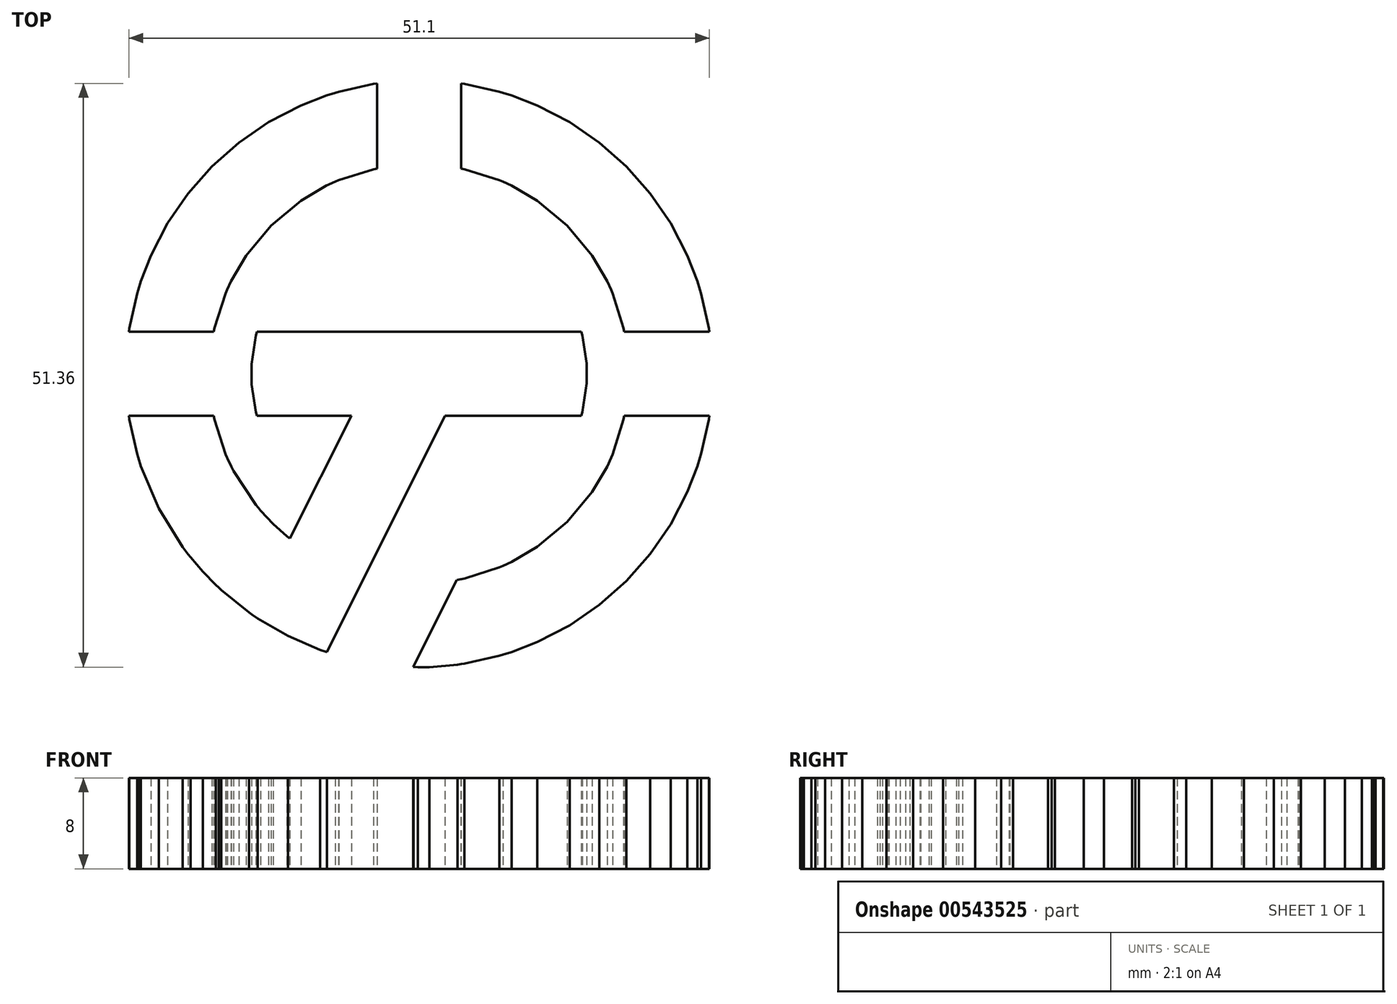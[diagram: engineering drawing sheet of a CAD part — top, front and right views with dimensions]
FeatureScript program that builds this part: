
annotation { "Feature Type Name" : "Feature", "Feature Type Description" : "" }
export const myFeature = defineFeature(function(context is Context, id is Id, definition is map)
    precondition{}
    {
        {
            var Q0;
            Q0=qCreatedBy(makeId("Top.planeOp"),FACE);
            var sketch = newSketch(context, id + "F0", { "sketchPlane" : qUnion([Q0])});
            skLineSegment(sketch, "E0", {"start": v(16.9, -7.24) * mm, "end": v(16.55, -8.03) * mm});
            skLineSegment(sketch, "E1", {"start": v(16.55, -8.03) * mm, "end": v(15.22, -10.26) * mm});
            skLineSegment(sketch, "E2", {"start": v(15.22, -10.26) * mm, "end": v(13.03, -12.9) * mm});
            skLineSegment(sketch, "E3", {"start": v(13.03, -12.9) * mm, "end": v(10.4, -15.09) * mm});
            skLineSegment(sketch, "E4", {"start": v(10.4, -15.09) * mm, "end": v(8.16, -16.42) * mm});
            skLineSegment(sketch, "E5", {"start": v(8.16, -16.42) * mm, "end": v(7.37, -16.76) * mm});
            skLineSegment(sketch, "E6", {"start": v(7.37, -16.76) * mm, "end": v(7.08, -16.9) * mm});
            skLineSegment(sketch, "E7", {"start": v(7.08, -16.9) * mm, "end": v(4, -17.87) * mm});
            skLineSegment(sketch, "E8", {"start": v(4, -17.87) * mm, "end": v(3.69, -17.93) * mm});
            skLineSegment(sketch, "E9", {"start": v(3.69, -17.93) * mm, "end": v(3.66, -17.94) * mm});
            skLineSegment(sketch, "E10", {"start": v(3.66, -17.94) * mm, "end": v(3.34, -18) * mm});
            skLineSegment(sketch, "E11", {"start": v(3.34, -18) * mm, "end": v(3.31, -18) * mm});
            skLineSegment(sketch, "E12", {"start": v(3.31, -18) * mm, "end": v(-0.53, -25.67) * mm});
            skLineSegment(sketch, "E13", {"start": v(-0.53, -25.67) * mm, "end": v(-0.49, -25.67) * mm});
            skLineSegment(sketch, "E14", {"start": v(-0.49, -25.67) * mm, "end": v(-0.12, -25.68) * mm});
            skLineSegment(sketch, "E15", {"start": v(-0.12, -25.68) * mm, "end": v(0, -25.68) * mm});
            skLineSegment(sketch, "E16", {"start": v(0, -25.68) * mm, "end": v(0.92, -25.68) * mm});
            skLineSegment(sketch, "E17", {"start": v(0.92, -25.68) * mm, "end": v(3.39, -25.46) * mm});
            skLineSegment(sketch, "E18", {"start": v(3.39, -25.46) * mm, "end": v(3.69, -25.42) * mm});
            skLineSegment(sketch, "E19", {"start": v(3.69, -25.42) * mm, "end": v(4, -25.37) * mm});
            skLineSegment(sketch, "E20", {"start": v(4, -25.37) * mm, "end": v(7.07, -24.69) * mm});
            skLineSegment(sketch, "E21", {"start": v(7.07, -24.69) * mm, "end": v(7.37, -24.6) * mm});
            skLineSegment(sketch, "E22", {"start": v(7.37, -24.6) * mm, "end": v(8.15, -24.37) * mm});
            skLineSegment(sketch, "E23", {"start": v(8.15, -24.37) * mm, "end": v(10.4, -23.48) * mm});
            skLineSegment(sketch, "E24", {"start": v(10.4, -23.48) * mm, "end": v(13.25, -22) * mm});
            skLineSegment(sketch, "E25", {"start": v(13.25, -22) * mm, "end": v(15.87, -20.21) * mm});
            skLineSegment(sketch, "E26", {"start": v(15.87, -20.21) * mm, "end": v(18.24, -18.1) * mm});
            skLineSegment(sketch, "E27", {"start": v(18.24, -18.1) * mm, "end": v(20.34, -15.73) * mm});
            skLineSegment(sketch, "E28", {"start": v(20.34, -15.73) * mm, "end": v(22.14, -13.11) * mm});
            skLineSegment(sketch, "E29", {"start": v(22.14, -13.11) * mm, "end": v(23.61, -10.27) * mm});
            skLineSegment(sketch, "E30", {"start": v(23.61, -10.27) * mm, "end": v(24.5, -8.02) * mm});
            skLineSegment(sketch, "E31", {"start": v(24.5, -8.02) * mm, "end": v(24.73, -7.24) * mm});
            skLineSegment(sketch, "E32", {"start": v(24.73, -7.24) * mm, "end": v(24.82, -6.94) * mm});
            skLineSegment(sketch, "E33", {"start": v(24.82, -6.94) * mm, "end": v(25.5, -3.87) * mm});
            skLineSegment(sketch, "E34", {"start": v(25.5, -3.87) * mm, "end": v(25.55, -3.56) * mm});
            skLineSegment(sketch, "E35", {"start": v(25.55, -3.56) * mm, "end": v(18.07, -3.56) * mm});
            skLineSegment(sketch, "E36", {"start": v(18.07, -3.56) * mm, "end": v(18, -3.88) * mm});
            skLineSegment(sketch, "E37", {"start": v(18, -3.88) * mm, "end": v(17.02, -6.95) * mm});
            skLineSegment(sketch, "E38", {"start": v(17.02, -6.95) * mm, "end": v(16.9, -7.24) * mm});
            skLineSegment(sketch, "E39", {"start": v(16.9, 7.5) * mm, "end": v(17.02, 7.21) * mm});
            skLineSegment(sketch, "E40", {"start": v(17.02, 7.21) * mm, "end": v(18, 4.14) * mm});
            skLineSegment(sketch, "E41", {"start": v(18, 4.14) * mm, "end": v(18.07, 3.82) * mm});
            skLineSegment(sketch, "E42", {"start": v(18.07, 3.82) * mm, "end": v(25.55, 3.82) * mm});
            skLineSegment(sketch, "E43", {"start": v(25.55, 3.82) * mm, "end": v(25.5, 4.13) * mm});
            skLineSegment(sketch, "E44", {"start": v(25.5, 4.13) * mm, "end": v(24.82, 7.2) * mm});
            skLineSegment(sketch, "E45", {"start": v(24.82, 7.2) * mm, "end": v(24.73, 7.5) * mm});
            skLineSegment(sketch, "E46", {"start": v(24.73, 7.5) * mm, "end": v(24.5, 8.28) * mm});
            skLineSegment(sketch, "E47", {"start": v(24.5, 8.28) * mm, "end": v(23.61, 10.54) * mm});
            skLineSegment(sketch, "E48", {"start": v(23.61, 10.54) * mm, "end": v(22.14, 13.38) * mm});
            skLineSegment(sketch, "E49", {"start": v(22.14, 13.38) * mm, "end": v(20.34, 16) * mm});
            skLineSegment(sketch, "E50", {"start": v(20.34, 16) * mm, "end": v(18.24, 18.37) * mm});
            skLineSegment(sketch, "E51", {"start": v(18.24, 18.37) * mm, "end": v(15.87, 20.47) * mm});
            skLineSegment(sketch, "E52", {"start": v(15.87, 20.47) * mm, "end": v(13.25, 22.27) * mm});
            skLineSegment(sketch, "E53", {"start": v(13.25, 22.27) * mm, "end": v(10.4, 23.74) * mm});
            skLineSegment(sketch, "E54", {"start": v(10.4, 23.74) * mm, "end": v(8.15, 24.63) * mm});
            skLineSegment(sketch, "E55", {"start": v(8.15, 24.63) * mm, "end": v(7.37, 24.86) * mm});
            skLineSegment(sketch, "E56", {"start": v(7.37, 24.86) * mm, "end": v(7.07, 24.95) * mm});
            skLineSegment(sketch, "E57", {"start": v(7.07, 24.95) * mm, "end": v(4, 25.63) * mm});
            skLineSegment(sketch, "E58", {"start": v(4, 25.63) * mm, "end": v(3.69, 25.68) * mm});
            skLineSegment(sketch, "E59", {"start": v(3.69, 25.68) * mm, "end": v(3.69, 18.2) * mm});
            skLineSegment(sketch, "E60", {"start": v(3.69, 18.2) * mm, "end": v(4, 18.13) * mm});
            skLineSegment(sketch, "E61", {"start": v(4, 18.13) * mm, "end": v(7.08, 17.16) * mm});
            skLineSegment(sketch, "E62", {"start": v(7.08, 17.16) * mm, "end": v(7.37, 17.03) * mm});
            skLineSegment(sketch, "E63", {"start": v(7.37, 17.03) * mm, "end": v(8.16, 16.68) * mm});
            skLineSegment(sketch, "E64", {"start": v(8.16, 16.68) * mm, "end": v(10.4, 15.35) * mm});
            skLineSegment(sketch, "E65", {"start": v(10.4, 15.35) * mm, "end": v(13.03, 13.16) * mm});
            skLineSegment(sketch, "E66", {"start": v(13.03, 13.16) * mm, "end": v(15.22, 10.52) * mm});
            skLineSegment(sketch, "E67", {"start": v(15.22, 10.52) * mm, "end": v(16.55, 8.3) * mm});
            skLineSegment(sketch, "E68", {"start": v(16.55, 8.3) * mm, "end": v(16.9, 7.5) * mm});
            skLineSegment(sketch, "E69", {"start": v(2.29, -3.55) * mm, "end": v(14.28, -3.55) * mm});
            skLineSegment(sketch, "E70", {"start": v(14.28, -3.55) * mm, "end": v(14.36, -3.26) * mm});
            skLineSegment(sketch, "E71", {"start": v(14.36, -3.26) * mm, "end": v(14.75, -0.72) * mm});
            skLineSegment(sketch, "E72", {"start": v(14.75, -0.72) * mm, "end": v(14.75, 0.13) * mm});
            skLineSegment(sketch, "E73", {"start": v(14.75, 0.13) * mm, "end": v(14.75, 1.05) * mm});
            skLineSegment(sketch, "E74", {"start": v(14.75, 1.05) * mm, "end": v(14.36, 3.52) * mm});
            skLineSegment(sketch, "E75", {"start": v(14.36, 3.52) * mm, "end": v(14.28, 3.82) * mm});
            skLineSegment(sketch, "E76", {"start": v(14.28, 3.82) * mm, "end": v(-14.28, 3.82) * mm});
            skLineSegment(sketch, "E77", {"start": v(-14.28, 3.82) * mm, "end": v(-14.36, 3.52) * mm});
            skLineSegment(sketch, "E78", {"start": v(-14.36, 3.52) * mm, "end": v(-14.75, 0.98) * mm});
            skLineSegment(sketch, "E79", {"start": v(-14.75, 0.98) * mm, "end": v(-14.75, 0.13) * mm});
            skLineSegment(sketch, "E80", {"start": v(-14.75, 0.13) * mm, "end": v(-14.75, -0.8) * mm});
            skLineSegment(sketch, "E81", {"start": v(-14.75, -0.8) * mm, "end": v(-14.36, -3.26) * mm});
            skLineSegment(sketch, "E82", {"start": v(-14.36, -3.26) * mm, "end": v(-14.28, -3.55) * mm});
            skLineSegment(sketch, "E83", {"start": v(-14.28, -3.55) * mm, "end": v(-5.96, -3.55) * mm});
            skLineSegment(sketch, "E84", {"start": v(-5.96, -3.55) * mm, "end": v(-11.37, -14.36) * mm});
            skLineSegment(sketch, "E85", {"start": v(-11.37, -14.36) * mm, "end": v(-11.63, -14.16) * mm});
            skLineSegment(sketch, "E86", {"start": v(-11.63, -14.16) * mm, "end": v(-12.83, -13.1) * mm});
            skLineSegment(sketch, "E87", {"start": v(-12.83, -13.1) * mm, "end": v(-13.94, -11.92) * mm});
            skLineSegment(sketch, "E88", {"start": v(-13.94, -11.92) * mm, "end": v(-14.15, -11.68) * mm});
            skLineSegment(sketch, "E89", {"start": v(-14.15, -11.68) * mm, "end": v(-14.38, -11.4) * mm});
            skLineSegment(sketch, "E90", {"start": v(-14.38, -11.4) * mm, "end": v(-16.33, -8.42) * mm});
            skLineSegment(sketch, "E91", {"start": v(-16.33, -8.42) * mm, "end": v(-16.5, -8.1) * mm});
            skLineSegment(sketch, "E92", {"start": v(-16.5, -8.1) * mm, "end": v(-16.53, -8.03) * mm});
            skLineSegment(sketch, "E93", {"start": v(-16.53, -8.03) * mm, "end": v(-16.86, -7.31) * mm});
            skLineSegment(sketch, "E94", {"start": v(-16.86, -7.31) * mm, "end": v(-16.9, -7.24) * mm});
            skLineSegment(sketch, "E95", {"start": v(-16.9, -7.24) * mm, "end": v(-17.02, -6.95) * mm});
            skLineSegment(sketch, "E96", {"start": v(-17.02, -6.95) * mm, "end": v(-18, -3.87) * mm});
            skLineSegment(sketch, "E97", {"start": v(-18, -3.87) * mm, "end": v(-18.07, -3.55) * mm});
            skLineSegment(sketch, "E98", {"start": v(-18.07, -3.55) * mm, "end": v(-25.55, -3.55) * mm});
            skLineSegment(sketch, "E99", {"start": v(-25.55, -3.55) * mm, "end": v(-25.5, -3.87) * mm});
            skLineSegment(sketch, "E100", {"start": v(-25.5, -3.87) * mm, "end": v(-24.82, -6.94) * mm});
            skLineSegment(sketch, "E101", {"start": v(-24.82, -6.94) * mm, "end": v(-24.73, -7.24) * mm});
            skLineSegment(sketch, "E102", {"start": v(-24.73, -7.24) * mm, "end": v(-24.5, -8.03) * mm});
            skLineSegment(sketch, "E103", {"start": v(-24.5, -8.03) * mm, "end": v(-22.91, -11.73) * mm});
            skLineSegment(sketch, "E104", {"start": v(-22.91, -11.73) * mm, "end": v(-20.81, -15.13) * mm});
            skLineSegment(sketch, "E105", {"start": v(-20.81, -15.13) * mm, "end": v(-20.32, -15.76) * mm});
            skLineSegment(sketch, "E106", {"start": v(-20.32, -15.76) * mm, "end": v(-20.12, -16.02) * mm});
            skLineSegment(sketch, "E107", {"start": v(-20.12, -16.02) * mm, "end": v(-19.04, -17.27) * mm});
            skLineSegment(sketch, "E108", {"start": v(-19.04, -17.27) * mm, "end": v(-17.9, -18.45) * mm});
            skLineSegment(sketch, "E109", {"start": v(-17.9, -18.45) * mm, "end": v(-17.65, -18.67) * mm});
            skLineSegment(sketch, "E110", {"start": v(-17.65, -18.67) * mm, "end": v(-17.42, -18.89) * mm});
            skLineSegment(sketch, "E111", {"start": v(-17.42, -18.89) * mm, "end": v(-14.97, -20.88) * mm});
            skLineSegment(sketch, "E112", {"start": v(-14.97, -20.88) * mm, "end": v(-14.72, -21.06) * mm});
            skLineSegment(sketch, "E113", {"start": v(-14.72, -21.06) * mm, "end": v(-14.21, -21.4) * mm});
            skLineSegment(sketch, "E114", {"start": v(-14.21, -21.4) * mm, "end": v(-11.55, -22.94) * mm});
            skLineSegment(sketch, "E115", {"start": v(-11.55, -22.94) * mm, "end": v(-8.71, -24.17) * mm});
            skLineSegment(sketch, "E116", {"start": v(-8.71, -24.17) * mm, "end": v(-8.12, -24.37) * mm});
            skLineSegment(sketch, "E117", {"start": v(-8.12, -24.37) * mm, "end": v(2.29, -3.55) * mm});
            skLineSegment(sketch, "E118", {"start": v(-16.9, 7.5) * mm, "end": v(-16.55, 8.3) * mm});
            skLineSegment(sketch, "E119", {"start": v(-16.55, 8.3) * mm, "end": v(-15.22, 10.52) * mm});
            skLineSegment(sketch, "E120", {"start": v(-15.22, 10.52) * mm, "end": v(-13.03, 13.16) * mm});
            skLineSegment(sketch, "E121", {"start": v(-13.03, 13.16) * mm, "end": v(-10.4, 15.35) * mm});
            skLineSegment(sketch, "E122", {"start": v(-10.4, 15.35) * mm, "end": v(-8.16, 16.68) * mm});
            skLineSegment(sketch, "E123", {"start": v(-8.16, 16.68) * mm, "end": v(-7.37, 17.03) * mm});
            skLineSegment(sketch, "E124", {"start": v(-7.37, 17.03) * mm, "end": v(-7.08, 17.16) * mm});
            skLineSegment(sketch, "E125", {"start": v(-7.08, 17.16) * mm, "end": v(-4, 18.13) * mm});
            skLineSegment(sketch, "E126", {"start": v(-4, 18.13) * mm, "end": v(-3.69, 18.2) * mm});
            skLineSegment(sketch, "E127", {"start": v(-3.69, 18.2) * mm, "end": v(-3.69, 25.68) * mm});
            skLineSegment(sketch, "E128", {"start": v(-3.69, 25.68) * mm, "end": v(-4, 25.63) * mm});
            skLineSegment(sketch, "E129", {"start": v(-4, 25.63) * mm, "end": v(-7.08, 24.95) * mm});
            skLineSegment(sketch, "E130", {"start": v(-7.08, 24.95) * mm, "end": v(-7.37, 24.86) * mm});
            skLineSegment(sketch, "E131", {"start": v(-7.37, 24.86) * mm, "end": v(-8.15, 24.63) * mm});
            skLineSegment(sketch, "E132", {"start": v(-8.15, 24.63) * mm, "end": v(-10.4, 23.74) * mm});
            skLineSegment(sketch, "E133", {"start": v(-10.4, 23.74) * mm, "end": v(-13.25, 22.27) * mm});
            skLineSegment(sketch, "E134", {"start": v(-13.25, 22.27) * mm, "end": v(-15.87, 20.47) * mm});
            skLineSegment(sketch, "E135", {"start": v(-15.87, 20.47) * mm, "end": v(-18.24, 18.37) * mm});
            skLineSegment(sketch, "E136", {"start": v(-18.24, 18.37) * mm, "end": v(-20.34, 16) * mm});
            skLineSegment(sketch, "E137", {"start": v(-20.34, 16) * mm, "end": v(-22.14, 13.38) * mm});
            skLineSegment(sketch, "E138", {"start": v(-22.14, 13.38) * mm, "end": v(-23.61, 10.54) * mm});
            skLineSegment(sketch, "E139", {"start": v(-23.61, 10.54) * mm, "end": v(-24.5, 8.28) * mm});
            skLineSegment(sketch, "E140", {"start": v(-24.5, 8.28) * mm, "end": v(-24.73, 7.5) * mm});
            skLineSegment(sketch, "E141", {"start": v(-24.73, 7.5) * mm, "end": v(-24.82, 7.2) * mm});
            skLineSegment(sketch, "E142", {"start": v(-24.82, 7.2) * mm, "end": v(-25.5, 4.13) * mm});
            skLineSegment(sketch, "E143", {"start": v(-25.5, 4.13) * mm, "end": v(-25.55, 3.82) * mm});
            skLineSegment(sketch, "E144", {"start": v(-25.55, 3.82) * mm, "end": v(-18.07, 3.82) * mm});
            skLineSegment(sketch, "E145", {"start": v(-18.07, 3.82) * mm, "end": v(-18, 4.14) * mm});
            skLineSegment(sketch, "E146", {"start": v(-18, 4.14) * mm, "end": v(-17.02, 7.21) * mm});
            skLineSegment(sketch, "E147", {"start": v(-17.02, 7.21) * mm, "end": v(-16.9, 7.5) * mm});
            skSolve(sketch);
        }
        {
            var Q0;
            Q0=makeQuery(id+"F0.imprint","IMPRINT",FACE,{"disambiguationData":[TD([[makeQuery(id+"F0.imprint","IMPRINT",EDGE,{"derivedFrom":sQuery(id+"F0.wireOp",EDGE,"E118")}),1.0]])]});
            var Q1;
            Q1=makeQuery(id+"F0.imprint","IMPRINT",FACE,{"disambiguationData":[TD([[makeQuery(id+"F0.imprint","IMPRINT",EDGE,{"derivedFrom":sQuery(id+"F0.wireOp",EDGE,"E69")}),1.0]])]});
            var Q2;
            Q2=makeQuery(id+"F0.imprint","IMPRINT",FACE,{"disambiguationData":[TD([[makeQuery(id+"F0.imprint","IMPRINT",EDGE,{"derivedFrom":sQuery(id+"F0.wireOp",EDGE,"E39")}),1.0]])]});
            var Q3;
            Q3=makeQuery(id+"F0.imprint","IMPRINT",FACE,{"disambiguationData":[TD([[makeQuery(id+"F0.imprint","IMPRINT",EDGE,{"derivedFrom":sQuery(id+"F0.wireOp",EDGE,"E0")}),1.0]])]});
            extrude(context, id + "F1", {"entities" : qUnion([Q0, Q1, Q2, Q3]), "depth" : 8 * mm, "offsetDistance" : 25 * mm});
        }
    });
